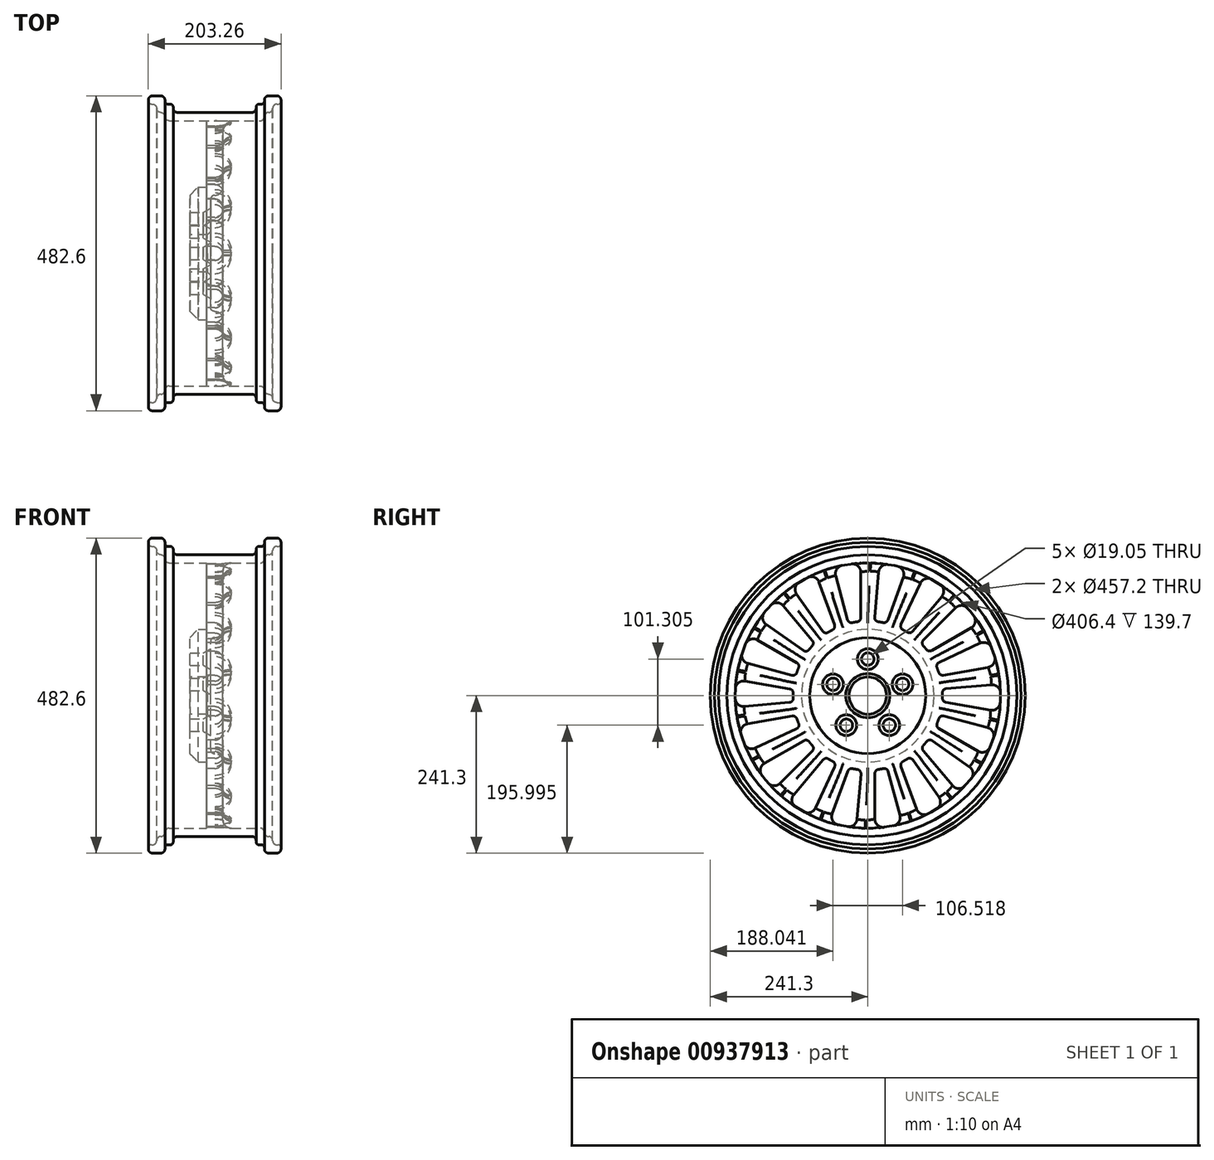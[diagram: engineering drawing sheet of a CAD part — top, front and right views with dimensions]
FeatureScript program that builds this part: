
annotation { "Feature Type Name" : "Feature", "Feature Type Description" : "" }
export const myFeature = defineFeature(function(context is Context, id is Id, definition is map)
    precondition{}
    {
        {
            var Q0;
            Q0=qCreatedBy(makeId("Front.planeOp"),FACE);
            var sketch = newSketch(context, id + "F0", { "sketchPlane" : qUnion([Q0])});
            skLineSegment(sketch, "E0", {"start": v(12.7, 101.6) * mm, "end": v(12.7, 203.2) * mm});
            skLineSegment(sketch, "E1", {"start": v(95.25, 241.3) * mm, "end": v(82.55, 241.3) * mm});
            skLineSegment(sketch, "E2", {"start": v(76.2, 234.95) * mm, "end": v(76.2, 233.05) * mm});
            skLineSegment(sketch, "E3", {"start": v(71.75, 228.6) * mm, "end": v(67.95, 228.6) * mm});
            skLineSegment(sketch, "E4", {"start": v(63.5, 224.16) * mm, "end": v(63.5, 222.25) * mm});
            skPoint(sketch, "E5.visualSharp", {"position": v(63.5, 215.9) * mm});
            skArc(sketch, "E5.filletArc", {"start": v(57.15, 215.9) * mm, "mid": v(61.64, 217.76) * mm, "end": v(63.5, 222.25) * mm});
            skPoint(sketch, "E6.visualSharp", {"position": v(63.5, 228.6) * mm});
            skArc(sketch, "E6.filletArc", {"start": v(67.95, 228.6) * mm, "mid": v(64.8, 227.3) * mm, "end": v(63.5, 224.16) * mm});
            skPoint(sketch, "E7.visualSharp", {"position": v(76.2, 228.6) * mm});
            skArc(sketch, "E7.filletArc", {"start": v(71.75, 228.6) * mm, "mid": v(74.9, 229.9) * mm, "end": v(76.2, 233.05) * mm});
            skPoint(sketch, "E8.visualSharp", {"position": v(76.2, 241.3) * mm});
            skArc(sketch, "E8.filletArc", {"start": v(82.55, 241.3) * mm, "mid": v(78.06, 239.44) * mm, "end": v(76.2, 234.95) * mm});
            skPoint(sketch, "E9.visualSharp", {"position": v(101.6, 241.3) * mm});
            skArc(sketch, "E9.filletArc", {"start": v(101.6, 234.95) * mm, "mid": v(99.74, 239.44) * mm, "end": v(95.25, 241.3) * mm});
            skLineSegment(sketch, "E10", {"start": v(12.7, 203.2) * mm, "end": v(69.85, 203.2) * mm});
            skLineSegment(sketch, "E11", {"start": v(76.2, 209.55) * mm, "end": v(76.2, 209.55) * mm});
            skLineSegment(sketch, "E12", {"start": v(82.55, 215.9) * mm, "end": v(82.55, 215.9) * mm});
            skPoint(sketch, "E12.endSnap0", {"position": v(88.9, 241.3) * mm});
            skLineSegment(sketch, "E13", {"start": v(88.9, 222.25) * mm, "end": v(88.9, 222.25) * mm});
            skLineSegment(sketch, "E14", {"start": v(95.25, 228.6) * mm, "end": v(97.18, 228.6) * mm});
            skLineSegment(sketch, "E15", {"start": v(101.63, 233.1) * mm, "end": v(101.6, 234.95) * mm});
            skPoint(sketch, "E16.visualSharp", {"position": v(76.2, 203.2) * mm});
            skArc(sketch, "E16.filletArc", {"start": v(69.85, 203.2) * mm, "mid": v(74.34, 205.06) * mm, "end": v(76.2, 209.55) * mm});
            skPoint(sketch, "E17.visualSharp", {"position": v(88.9, 215.9) * mm});
            skArc(sketch, "E17.filletArc", {"start": v(82.55, 215.9) * mm, "mid": v(87.04, 217.76) * mm, "end": v(88.9, 222.25) * mm});
            skPoint(sketch, "E18.visualSharp", {"position": v(88.9, 228.6) * mm});
            skArc(sketch, "E18.filletArc", {"start": v(95.25, 228.6) * mm, "mid": v(90.76, 226.74) * mm, "end": v(88.9, 222.25) * mm});
            skPoint(sketch, "E19.visualSharp", {"position": v(76.2, 215.9) * mm});
            skArc(sketch, "E19.filletArc", {"start": v(82.55, 215.9) * mm, "mid": v(78.06, 214.04) * mm, "end": v(76.2, 209.55) * mm});
            skPoint(sketch, "E20.visualSharp", {"position": v(101.7, 228.6) * mm});
            skArc(sketch, "E20.filletArc", {"start": v(97.18, 228.6) * mm, "mid": v(100.35, 229.92) * mm, "end": v(101.63, 233.1) * mm});
            skArc(sketch, "E21.MirrorCS", {"start": v(-82.55, 215.9) * mm, "mid": v(-87.04, 217.76) * mm, "end": v(-88.9, 222.25) * mm});
            skArc(sketch, "E22.MirrorCS", {"start": v(-71.75, 228.6) * mm, "mid": v(-74.9, 229.9) * mm, "end": v(-76.2, 233.05) * mm});
            skLineSegment(sketch, "E23.MirrorCS", {"start": v(-63.5, 224.16) * mm, "end": v(-63.5, 222.25) * mm});
            skLineSegment(sketch, "E24.MirrorCS", {"start": v(-76.2, 234.95) * mm, "end": v(-76.2, 233.05) * mm});
            skArc(sketch, "E25.MirrorCS", {"start": v(-97.18, 228.6) * mm, "mid": v(-100.35, 229.92) * mm, "end": v(-101.63, 233.1) * mm});
            skArc(sketch, "E26.MirrorCS", {"start": v(-95.25, 228.6) * mm, "mid": v(-90.76, 226.74) * mm, "end": v(-88.9, 222.25) * mm});
            skLineSegment(sketch, "E27.MirrorCS", {"start": v(-101.63, 233.1) * mm, "end": v(-101.6, 234.95) * mm});
            skLineSegment(sketch, "E28.MirrorCS", {"start": v(-95.25, 228.6) * mm, "end": v(-97.18, 228.6) * mm});
            skArc(sketch, "E29.MirrorCS", {"start": v(-69.85, 203.2) * mm, "mid": v(-74.34, 205.06) * mm, "end": v(-76.2, 209.55) * mm});
            skArc(sketch, "E30.MirrorCS", {"start": v(-101.6, 234.95) * mm, "mid": v(-99.74, 239.44) * mm, "end": v(-95.25, 241.3) * mm});
            skLineSegment(sketch, "E31.MirrorCS", {"start": v(-71.75, 228.6) * mm, "end": v(-67.95, 228.6) * mm});
            skArc(sketch, "E32.MirrorCS", {"start": v(-82.55, 215.9) * mm, "mid": v(-78.06, 214.04) * mm, "end": v(-76.2, 209.55) * mm});
            skArc(sketch, "E33.MirrorCS", {"start": v(-82.55, 241.3) * mm, "mid": v(-78.06, 239.44) * mm, "end": v(-76.2, 234.95) * mm});
            skLineSegment(sketch, "E34.MirrorCS", {"start": v(-95.25, 241.3) * mm, "end": v(-82.55, 241.3) * mm});
            skArc(sketch, "E35.MirrorCS", {"start": v(-67.95, 228.6) * mm, "mid": v(-64.8, 227.3) * mm, "end": v(-63.5, 224.16) * mm});
            skArc(sketch, "E36.MirrorCS", {"start": v(-57.15, 215.9) * mm, "mid": v(-61.64, 217.76) * mm, "end": v(-63.5, 222.25) * mm});
            skLineSegment(sketch, "E37.MirrorCS", {"start": v(-82.55, 215.9) * mm, "end": v(-82.55, 215.9) * mm});
            skPoint(sketch, "E38.MirrorP", {"position": v(-63.5, 215.9) * mm});
            skPoint(sketch, "E39.MirrorP", {"position": v(-88.9, 215.9) * mm});
            skPoint(sketch, "E40.MirrorP", {"position": v(-76.2, 215.9) * mm});
            skPoint(sketch, "E41.MirrorP", {"position": v(-88.9, 228.6) * mm});
            skPoint(sketch, "E42.MirrorP", {"position": v(-76.2, 228.6) * mm});
            skPoint(sketch, "E43.MirrorP", {"position": v(-76.2, 241.3) * mm});
            skLineSegment(sketch, "E44.MirrorCS", {"start": v(-12.7, 101.6) * mm, "end": v(-12.7, 203.2) * mm});
            skPoint(sketch, "E45.MirrorP", {"position": v(-76.2, 203.2) * mm});
            skLineSegment(sketch, "E46.MirrorCS", {"start": v(-88.9, 222.25) * mm, "end": v(-88.9, 222.25) * mm});
            skPoint(sketch, "E47.MirrorP", {"position": v(-101.7, 228.6) * mm});
            skLineSegment(sketch, "E48.MirrorCS", {"start": v(-12.7, 203.2) * mm, "end": v(-69.85, 203.2) * mm});
            skPoint(sketch, "E49.MirrorP", {"position": v(-101.6, 241.3) * mm});
            skPoint(sketch, "E50.MirrorP", {"position": v(-63.5, 228.6) * mm});
            skPoint(sketch, "E51.MirrorP", {"position": v(-88.9, 241.3) * mm});
            skLineSegment(sketch, "E52.MirrorCS", {"start": v(-76.2, 209.55) * mm, "end": v(-76.2, 209.55) * mm});
            skLineSegment(sketch, "E53", {"start": v(-38.1, 28.65) * mm, "end": v(-38.1, 101.6) * mm});
            skLineSegment(sketch, "E54", {"start": v(-38.1, 101.6) * mm, "end": v(-12.7, 101.6) * mm});
            skPoint(sketch, "E55.orphan", {"position": v(0, 0) * mm});
            skLineSegment(sketch, "E56.trimOffspring", {"start": v(0, 88.9) * mm, "end": v(0, 88.9) * mm});
            skLineSegment(sketch, "E57", {"start": v(-6.35, 28.57) * mm, "end": v(-6.35, 82.55) * mm});
            skPoint(sketch, "E58.newPointA", {"position": v(-6.35, 88.9) * mm});
            skPoint(sketch, "E58.newPointB", {"position": v(-4.35, 88.9) * mm});
            skArc(sketch, "E58.filletArc", {"start": v(0, 88.9) * mm, "mid": v(-4.5, 87.04) * mm, "end": v(-6.35, 82.55) * mm});
            skPoint(sketch, "E59.visualSharp", {"position": v(12.7, 88.9) * mm});
            skArc(sketch, "E59.filletArc", {"start": v(0, 88.9) * mm, "mid": v(8.98, 92.62) * mm, "end": v(12.7, 101.6) * mm});
            skLineSegment(sketch, "E60", {"start": v(-6.35, 28.57) * mm, "end": v(-38.1, 28.65) * mm});
            skLineSegment(sketch, "E61", {"start": v(57.15, 215.9) * mm, "end": v(-57.15, 215.9) * mm});
            skLineSegment(sketch, "E62", {"start": v(0, 0) * mm, "end": v(-39.67, 0) * mm});
            skSolve(sketch);
        }
        {
            var Q0;
            Q0 = qSketchRegion(id + "F0", true);
            var Q1;
            Q1=sQuery(id+"F0.wireOp",EDGE,"E62");
            revolve(context, id + "F1", {"surfaceOperationType" : NewSurfaceOperationType.NEW, "entities" : qUnion([Q0]), "axis" : qUnion([Q1]), "revolveType" : RevolveType.FULL});
        }
        {
            var Q0;
            Q0=makeQuery(id+"F1.opRevolve","SWEPT_FACE",FACE,{"disambiguationData":[OSD([sQuery(id+"F0.wireOp",EDGE,"E44.MirrorCS")])]});
            var sketch = newSketch(context, id + "F2", { "sketchPlane" : qUnion([Q0])});
            skArc(sketch, "E63", {"start": v(39.39, 199.35) * mm, "mid": v(32.22, 200.63) * mm, "end": v(25.02, 201.65) * mm});
            skArc(sketch, "E64", {"start": v(23.73, 111.8) * mm, "mid": v(19.98, 112.54) * mm, "end": v(16.2, 113.15) * mm});
            skLineSegment(sketch, "E65", {"start": v(10.75, 189.05) * mm, "end": v(10.75, 119.43) * mm});
            skLineSegment(sketch, "E66", {"start": v(31.18, 116.38) * mm, "end": v(49.2, 183.6) * mm});
            skPoint(sketch, "E67.visualSharp", {"position": v(10.75, 113.8) * mm});
            skArc(sketch, "E67.filletArc", {"start": v(10.75, 119.43) * mm, "mid": v(12.3, 115.27) * mm, "end": v(16.2, 113.15) * mm});
            skPoint(sketch, "E68.visualSharp", {"position": v(29.58, 110.4) * mm});
            skArc(sketch, "E68.filletArc", {"start": v(23.73, 111.8) * mm, "mid": v(28.37, 112.6) * mm, "end": v(31.18, 116.38) * mm});
            skPoint(sketch, "E69.visualSharp", {"position": v(52.6, 196.28) * mm});
            skArc(sketch, "E69.filletArc", {"start": v(49.2, 183.6) * mm, "mid": v(47.7, 193.6) * mm, "end": v(39.39, 199.35) * mm});
            skPoint(sketch, "E70.visualSharp", {"position": v(10.75, 202.92) * mm});
            skArc(sketch, "E70.filletArc", {"start": v(25.02, 201.65) * mm, "mid": v(15.04, 198.57) * mm, "end": v(10.75, 189.05) * mm});
            skPoint(sketch, "E71.1.0", {"position": v(-28.82, 110.6) * mm});
            skLineSegment(sketch, "E71.1.1", {"start": v(-54.56, 181.33) * mm, "end": v(-30.74, 115.9) * mm});
            skPoint(sketch, "E71.1.2", {"position": v(-9.96, 113.87) * mm});
            skPoint(sketch, "E71.1.3", {"position": v(-59.3, 194.36) * mm});
            skLineSegment(sketch, "E71.1.4", {"start": v(-10.5, 120.02) * mm, "end": v(-16.57, 189.35) * mm});
            skPoint(sketch, "E71.1.5", {"position": v(-17.71, 202.43) * mm});
            skArc(sketch, "E71.1.6", {"start": v(-16.57, 189.35) * mm, "mid": v(-21.38, 198.24) * mm, "end": v(-31.17, 200.8) * mm});
            skArc(sketch, "E71.1.7", {"start": v(-45.46, 198.05) * mm, "mid": v(-53.78, 191.74) * mm, "end": v(-54.56, 181.33) * mm});
            skArc(sketch, "E71.1.8", {"start": v(-31.17, 200.8) * mm, "mid": v(-38.34, 199.55) * mm, "end": v(-45.46, 198.05) * mm});
            skArc(sketch, "E71.1.9", {"start": v(-30.74, 115.9) * mm, "mid": v(-27.86, 112.53) * mm, "end": v(-23.47, 111.86) * mm});
            skArc(sketch, "E71.1.10", {"start": v(-15.94, 113.18) * mm, "mid": v(-19.72, 112.59) * mm, "end": v(-23.47, 111.86) * mm});
            skArc(sketch, "E71.1.11", {"start": v(-15.94, 113.18) * mm, "mid": v(-11.86, 115.52) * mm, "end": v(-10.5, 120.02) * mm});
            skPoint(sketch, "E71.2.0", {"position": v(-64.9, 94.08) * mm});
            skLineSegment(sketch, "E71.2.1", {"start": v(-113.28, 151.73) * mm, "end": v(-68.53, 98.4) * mm});
            skPoint(sketch, "E71.2.2", {"position": v(-48.3, 103.6) * mm});
            skPoint(sketch, "E71.2.3", {"position": v(-122.2, 162.35) * mm});
            skLineSegment(sketch, "E71.2.4", {"start": v(-50.92, 109.2) * mm, "end": v(-80.33, 172.27) * mm});
            skPoint(sketch, "E71.2.5", {"position": v(-85.88, 184.16) * mm});
            skArc(sketch, "E71.2.6", {"start": v(-80.33, 172.27) * mm, "mid": v(-87.9, 178.97) * mm, "end": v(-97.96, 178.03) * mm});
            skArc(sketch, "E71.2.7", {"start": v(-110.46, 170.56) * mm, "mid": v(-116.11, 161.78) * mm, "end": v(-113.28, 151.73) * mm});
            skArc(sketch, "E71.2.8", {"start": v(-97.96, 178.03) * mm, "mid": v(-104.28, 174.4) * mm, "end": v(-110.46, 170.56) * mm});
            skArc(sketch, "E71.2.9", {"start": v(-68.53, 98.4) * mm, "mid": v(-64.67, 96.21) * mm, "end": v(-60.32, 97.09) * mm});
            skArc(sketch, "E71.2.10", {"start": v(-53.7, 100.9) * mm, "mid": v(-57.04, 99.05) * mm, "end": v(-60.32, 97.09) * mm});
            skArc(sketch, "E71.2.11", {"start": v(-53.7, 100.9) * mm, "mid": v(-50.65, 104.5) * mm, "end": v(-50.92, 109.2) * mm});
            skPoint(sketch, "E71.3.0", {"position": v(-93.17, 66.2) * mm});
            skLineSegment(sketch, "E71.3.1", {"start": v(-158.35, 103.84) * mm, "end": v(-98.06, 69.03) * mm});
            skPoint(sketch, "E71.3.2", {"position": v(-80.82, 80.82) * mm});
            skPoint(sketch, "E71.3.3", {"position": v(-170.35, 110.77) * mm});
            skLineSegment(sketch, "E71.3.4", {"start": v(-85.2, 85.2) * mm, "end": v(-134.4, 134.4) * mm});
            skPoint(sketch, "E71.3.5", {"position": v(-143.68, 143.68) * mm});
            skArc(sketch, "E71.3.6", {"start": v(-134.4, 134.4) * mm, "mid": v(-143.8, 138.12) * mm, "end": v(-152.94, 133.79) * mm});
            skArc(sketch, "E71.3.7", {"start": v(-162.13, 122.5) * mm, "mid": v(-164.44, 112.31) * mm, "end": v(-158.35, 103.84) * mm});
            skArc(sketch, "E71.3.8", {"start": v(-152.94, 133.79) * mm, "mid": v(-157.64, 128.22) * mm, "end": v(-162.13, 122.5) * mm});
            skArc(sketch, "E71.3.9", {"start": v(-98.06, 69.03) * mm, "mid": v(-93.68, 68.3) * mm, "end": v(-89.89, 70.6) * mm});
            skArc(sketch, "E71.3.10", {"start": v(-84.96, 76.46) * mm, "mid": v(-87.47, 73.57) * mm, "end": v(-89.89, 70.6) * mm});
            skArc(sketch, "E71.3.11", {"start": v(-84.96, 76.46) * mm, "mid": v(-83.34, 80.87) * mm, "end": v(-85.2, 85.2) * mm});
            skPoint(sketch, "E71.4.0", {"position": v(-110.2, 30.35) * mm});
            skLineSegment(sketch, "E71.4.1", {"start": v(-184.31, 43.42) * mm, "end": v(-115.75, 31.33) * mm});
            skPoint(sketch, "E71.4.2", {"position": v(-103.6, 48.3) * mm});
            skPoint(sketch, "E71.4.3", {"position": v(-197.97, 45.82) * mm});
            skLineSegment(sketch, "E71.4.4", {"start": v(-109.2, 50.92) * mm, "end": v(-172.27, 80.33) * mm});
            skPoint(sketch, "E71.4.5", {"position": v(-184.16, 85.88) * mm});
            skArc(sketch, "E71.4.6", {"start": v(-172.27, 80.33) * mm, "mid": v(-182.37, 80.6) * mm, "end": v(-189.48, 73.4) * mm});
            skArc(sketch, "E71.4.7", {"start": v(-194.25, 59.65) * mm, "mid": v(-192.94, 49.3) * mm, "end": v(-184.31, 43.42) * mm});
            skArc(sketch, "E71.4.8", {"start": v(-189.48, 73.4) * mm, "mid": v(-191.99, 66.57) * mm, "end": v(-194.25, 59.65) * mm});
            skArc(sketch, "E71.4.9", {"start": v(-115.75, 31.33) * mm, "mid": v(-111.38, 32.13) * mm, "end": v(-108.61, 35.6) * mm});
            skArc(sketch, "E71.4.10", {"start": v(-105.99, 42.79) * mm, "mid": v(-107.36, 39.22) * mm, "end": v(-108.61, 35.6) * mm});
            skArc(sketch, "E71.4.11", {"start": v(-105.99, 42.79) * mm, "mid": v(-105.97, 47.5) * mm, "end": v(-109.2, 50.92) * mm});
            skPoint(sketch, "E71.5.0", {"position": v(-113.93, -9.17) * mm});
            skLineSegment(sketch, "E71.5.1", {"start": v(-188.05, -22.24) * mm, "end": v(-119.48, -10.15) * mm});
            skPoint(sketch, "E71.5.2", {"position": v(-113.87, 9.96) * mm});
            skPoint(sketch, "E71.5.3", {"position": v(-201.7, -24.65) * mm});
            skLineSegment(sketch, "E71.5.4", {"start": v(-120.02, 10.5) * mm, "end": v(-189.35, 16.57) * mm});
            skPoint(sketch, "E71.5.5", {"position": v(-202.43, 17.71) * mm});
            skArc(sketch, "E71.5.6", {"start": v(-189.35, 16.57) * mm, "mid": v(-198.94, 13.37) * mm, "end": v(-203.16, 4.18) * mm});
            skArc(sketch, "E71.5.7", {"start": v(-202.93, -10.38) * mm, "mid": v(-198.16, -19.67) * mm, "end": v(-188.05, -22.24) * mm});
            skArc(sketch, "E71.5.8", {"start": v(-203.16, 4.18) * mm, "mid": v(-203.18, -3.1) * mm, "end": v(-202.93, -10.38) * mm});
            skArc(sketch, "E71.5.9", {"start": v(-119.48, -10.15) * mm, "mid": v(-115.66, -7.9) * mm, "end": v(-114.24, -3.7) * mm});
            skArc(sketch, "E71.5.10", {"start": v(-114.23, 3.96) * mm, "mid": v(-114.3, 0.13) * mm, "end": v(-114.24, -3.7) * mm});
            skArc(sketch, "E71.5.11", {"start": v(-114.23, 3.96) * mm, "mid": v(-115.82, 8.38) * mm, "end": v(-120.02, 10.5) * mm});
            skPoint(sketch, "E71.6.0", {"position": v(-103.92, -47.59) * mm});
            skLineSegment(sketch, "E71.6.1", {"start": v(-169.1, -85.21) * mm, "end": v(-108.8, -50.4) * mm});
            skPoint(sketch, "E71.6.2", {"position": v(-110.4, -29.58) * mm});
            skPoint(sketch, "E71.6.3", {"position": v(-181.1, -92.15) * mm});
            skLineSegment(sketch, "E71.6.4", {"start": v(-116.38, -31.18) * mm, "end": v(-183.6, -49.2) * mm});
            skPoint(sketch, "E71.6.5", {"position": v(-196.28, -52.6) * mm});
            skArc(sketch, "E71.6.6", {"start": v(-183.6, -49.2) * mm, "mid": v(-191.52, -55.48) * mm, "end": v(-192.33, -65.56) * mm});
            skArc(sketch, "E71.6.7", {"start": v(-187.15, -79.16) * mm, "mid": v(-179.49, -86.26) * mm, "end": v(-169.1, -85.21) * mm});
            skArc(sketch, "E71.6.8", {"start": v(-192.33, -65.56) * mm, "mid": v(-189.86, -72.4) * mm, "end": v(-187.15, -79.16) * mm});
            skArc(sketch, "E71.6.9", {"start": v(-108.8, -50.4) * mm, "mid": v(-105.98, -46.98) * mm, "end": v(-106.09, -42.54) * mm});
            skArc(sketch, "E71.6.10", {"start": v(-108.7, -35.35) * mm, "mid": v(-107.45, -38.97) * mm, "end": v(-106.09, -42.54) * mm});
            skArc(sketch, "E71.6.11", {"start": v(-108.7, -35.35) * mm, "mid": v(-111.7, -31.74) * mm, "end": v(-116.38, -31.18) * mm});
            skPoint(sketch, "E71.7.0", {"position": v(-81.38, -80.26) * mm});
            skLineSegment(sketch, "E71.7.1", {"start": v(-129.76, -137.91) * mm, "end": v(-85, -84.58) * mm});
            skPoint(sketch, "E71.7.2", {"position": v(-93.63, -65.56) * mm});
            skPoint(sketch, "E71.7.3", {"position": v(-138.67, -148.53) * mm});
            skLineSegment(sketch, "E71.7.4", {"start": v(-98.7, -69.1) * mm, "end": v(-155.7, -109.02) * mm});
            skPoint(sketch, "E71.7.5", {"position": v(-166.45, -116.55) * mm});
            skArc(sketch, "E71.7.6", {"start": v(-155.7, -109.02) * mm, "mid": v(-161, -117.64) * mm, "end": v(-158.31, -127.39) * mm});
            skArc(sketch, "E71.7.7", {"start": v(-148.78, -138.4) * mm, "mid": v(-139.16, -142.44) * mm, "end": v(-129.76, -137.91) * mm});
            skArc(sketch, "E71.7.8", {"start": v(-158.31, -127.39) * mm, "mid": v(-153.65, -132.98) * mm, "end": v(-148.78, -138.4) * mm});
            skArc(sketch, "E71.7.9", {"start": v(-85, -84.58) * mm, "mid": v(-83.52, -80.4) * mm, "end": v(-85.14, -76.26) * mm});
            skArc(sketch, "E71.7.10", {"start": v(-90.05, -70.4) * mm, "mid": v(-87.64, -73.37) * mm, "end": v(-85.14, -76.26) * mm});
            skArc(sketch, "E71.7.11", {"start": v(-90.05, -70.4) * mm, "mid": v(-94.11, -68.03) * mm, "end": v(-98.7, -69.1) * mm});
            skPoint(sketch, "E71.8.0", {"position": v(-49.02, -103.25) * mm});
            skLineSegment(sketch, "E71.8.1", {"start": v(-74.76, -173.97) * mm, "end": v(-50.95, -108.55) * mm});
            skPoint(sketch, "E71.8.2", {"position": v(-65.56, -93.63) * mm});
            skPoint(sketch, "E71.8.3", {"position": v(-79.5, -187) * mm});
            skLineSegment(sketch, "E71.8.4", {"start": v(-69.1, -98.7) * mm, "end": v(-109.02, -155.7) * mm});
            skPoint(sketch, "E71.8.5", {"position": v(-116.55, -166.45) * mm});
            skArc(sketch, "E71.8.6", {"start": v(-109.02, -155.7) * mm, "mid": v(-111.05, -165.6) * mm, "end": v(-105.2, -173.85) * mm});
            skArc(sketch, "E71.8.7", {"start": v(-92.48, -180.94) * mm, "mid": v(-82.05, -181.45) * mm, "end": v(-74.76, -173.97) * mm});
            skArc(sketch, "E71.8.8", {"start": v(-105.2, -173.85) * mm, "mid": v(-98.9, -177.5) * mm, "end": v(-92.48, -180.94) * mm});
            skArc(sketch, "E71.8.9", {"start": v(-50.95, -108.55) * mm, "mid": v(-50.99, -104.11) * mm, "end": v(-53.92, -100.78) * mm});
            skArc(sketch, "E71.8.10", {"start": v(-60.54, -96.95) * mm, "mid": v(-57.26, -98.92) * mm, "end": v(-53.92, -100.78) * mm});
            skArc(sketch, "E71.8.11", {"start": v(-60.54, -96.95) * mm, "mid": v(-65.17, -96.11) * mm, "end": v(-69.1, -98.7) * mm});
            skPoint(sketch, "E71.9.0", {"position": v(-10.75, -113.8) * mm});
            skLineSegment(sketch, "E71.9.1", {"start": v(-10.75, -189.05) * mm, "end": v(-10.75, -119.43) * mm});
            skPoint(sketch, "E71.9.2", {"position": v(-29.58, -110.4) * mm});
            skPoint(sketch, "E71.9.3", {"position": v(-10.75, -202.92) * mm});
            skLineSegment(sketch, "E71.9.4", {"start": v(-31.18, -116.38) * mm, "end": v(-49.2, -183.6) * mm});
            skPoint(sketch, "E71.9.5", {"position": v(-52.6, -196.28) * mm});
            skArc(sketch, "E71.9.6", {"start": v(-49.2, -183.6) * mm, "mid": v(-47.7, -193.6) * mm, "end": v(-39.39, -199.35) * mm});
            skArc(sketch, "E71.9.7", {"start": v(-25.02, -201.65) * mm, "mid": v(-15.04, -198.57) * mm, "end": v(-10.75, -189.05) * mm});
            skArc(sketch, "E71.9.8", {"start": v(-39.39, -199.35) * mm, "mid": v(-32.22, -200.63) * mm, "end": v(-25.02, -201.65) * mm});
            skArc(sketch, "E71.9.9", {"start": v(-10.75, -119.43) * mm, "mid": v(-12.3, -115.27) * mm, "end": v(-16.2, -113.15) * mm});
            skArc(sketch, "E71.9.10", {"start": v(-23.73, -111.8) * mm, "mid": v(-19.98, -112.54) * mm, "end": v(-16.2, -113.15) * mm});
            skArc(sketch, "E71.9.11", {"start": v(-23.73, -111.8) * mm, "mid": v(-28.37, -112.6) * mm, "end": v(-31.18, -116.38) * mm});
            skPoint(sketch, "E71.10.0", {"position": v(28.82, -110.6) * mm});
            skLineSegment(sketch, "E71.10.1", {"start": v(54.56, -181.33) * mm, "end": v(30.74, -115.9) * mm});
            skPoint(sketch, "E71.10.2", {"position": v(9.96, -113.87) * mm});
            skPoint(sketch, "E71.10.3", {"position": v(59.3, -194.36) * mm});
            skLineSegment(sketch, "E71.10.4", {"start": v(10.5, -120.02) * mm, "end": v(16.57, -189.35) * mm});
            skPoint(sketch, "E71.10.5", {"position": v(17.71, -202.43) * mm});
            skArc(sketch, "E71.10.6", {"start": v(16.57, -189.35) * mm, "mid": v(21.38, -198.24) * mm, "end": v(31.17, -200.8) * mm});
            skArc(sketch, "E71.10.7", {"start": v(45.46, -198.05) * mm, "mid": v(53.78, -191.74) * mm, "end": v(54.56, -181.33) * mm});
            skArc(sketch, "E71.10.8", {"start": v(31.17, -200.8) * mm, "mid": v(38.34, -199.55) * mm, "end": v(45.46, -198.05) * mm});
            skArc(sketch, "E71.10.9", {"start": v(30.74, -115.9) * mm, "mid": v(27.86, -112.53) * mm, "end": v(23.47, -111.86) * mm});
            skArc(sketch, "E71.10.10", {"start": v(15.94, -113.18) * mm, "mid": v(19.72, -112.59) * mm, "end": v(23.47, -111.86) * mm});
            skArc(sketch, "E71.10.11", {"start": v(15.94, -113.18) * mm, "mid": v(11.86, -115.52) * mm, "end": v(10.5, -120.02) * mm});
            skPoint(sketch, "E71.11.0", {"position": v(64.9, -94.08) * mm});
            skLineSegment(sketch, "E71.11.1", {"start": v(113.28, -151.73) * mm, "end": v(68.53, -98.4) * mm});
            skPoint(sketch, "E71.11.2", {"position": v(48.3, -103.6) * mm});
            skPoint(sketch, "E71.11.3", {"position": v(122.2, -162.35) * mm});
            skLineSegment(sketch, "E71.11.4", {"start": v(50.92, -109.2) * mm, "end": v(80.33, -172.27) * mm});
            skPoint(sketch, "E71.11.5", {"position": v(85.88, -184.16) * mm});
            skArc(sketch, "E71.11.6", {"start": v(80.33, -172.27) * mm, "mid": v(87.9, -178.97) * mm, "end": v(97.96, -178.03) * mm});
            skArc(sketch, "E71.11.7", {"start": v(110.46, -170.56) * mm, "mid": v(116.11, -161.78) * mm, "end": v(113.28, -151.73) * mm});
            skArc(sketch, "E71.11.8", {"start": v(97.96, -178.03) * mm, "mid": v(104.28, -174.4) * mm, "end": v(110.46, -170.56) * mm});
            skArc(sketch, "E71.11.9", {"start": v(68.53, -98.4) * mm, "mid": v(64.67, -96.21) * mm, "end": v(60.32, -97.09) * mm});
            skArc(sketch, "E71.11.10", {"start": v(53.7, -100.9) * mm, "mid": v(57.04, -99.05) * mm, "end": v(60.32, -97.09) * mm});
            skArc(sketch, "E71.11.11", {"start": v(53.7, -100.9) * mm, "mid": v(50.65, -104.5) * mm, "end": v(50.92, -109.2) * mm});
            skPoint(sketch, "E71.12.0", {"position": v(93.17, -66.2) * mm});
            skLineSegment(sketch, "E71.12.1", {"start": v(158.35, -103.84) * mm, "end": v(98.06, -69.03) * mm});
            skPoint(sketch, "E71.12.2", {"position": v(80.82, -80.82) * mm});
            skPoint(sketch, "E71.12.3", {"position": v(170.35, -110.77) * mm});
            skLineSegment(sketch, "E71.12.4", {"start": v(85.2, -85.2) * mm, "end": v(134.4, -134.4) * mm});
            skPoint(sketch, "E71.12.5", {"position": v(143.68, -143.68) * mm});
            skArc(sketch, "E71.12.6", {"start": v(134.4, -134.4) * mm, "mid": v(143.8, -138.12) * mm, "end": v(152.94, -133.79) * mm});
            skArc(sketch, "E71.12.7", {"start": v(162.13, -122.5) * mm, "mid": v(164.44, -112.31) * mm, "end": v(158.35, -103.84) * mm});
            skArc(sketch, "E71.12.8", {"start": v(152.94, -133.79) * mm, "mid": v(157.64, -128.22) * mm, "end": v(162.13, -122.5) * mm});
            skArc(sketch, "E71.12.9", {"start": v(98.06, -69.03) * mm, "mid": v(93.68, -68.3) * mm, "end": v(89.89, -70.6) * mm});
            skArc(sketch, "E71.12.10", {"start": v(84.96, -76.46) * mm, "mid": v(87.47, -73.57) * mm, "end": v(89.89, -70.6) * mm});
            skArc(sketch, "E71.12.11", {"start": v(84.96, -76.46) * mm, "mid": v(83.34, -80.87) * mm, "end": v(85.2, -85.2) * mm});
            skPoint(sketch, "E71.13.0", {"position": v(110.2, -30.35) * mm});
            skLineSegment(sketch, "E71.13.1", {"start": v(184.31, -43.42) * mm, "end": v(115.75, -31.33) * mm});
            skPoint(sketch, "E71.13.2", {"position": v(103.6, -48.3) * mm});
            skPoint(sketch, "E71.13.3", {"position": v(197.97, -45.82) * mm});
            skLineSegment(sketch, "E71.13.4", {"start": v(109.2, -50.92) * mm, "end": v(172.27, -80.33) * mm});
            skPoint(sketch, "E71.13.5", {"position": v(184.16, -85.88) * mm});
            skArc(sketch, "E71.13.6", {"start": v(172.27, -80.33) * mm, "mid": v(182.37, -80.6) * mm, "end": v(189.48, -73.4) * mm});
            skArc(sketch, "E71.13.7", {"start": v(194.25, -59.65) * mm, "mid": v(192.94, -49.3) * mm, "end": v(184.31, -43.42) * mm});
            skArc(sketch, "E71.13.8", {"start": v(189.48, -73.4) * mm, "mid": v(191.99, -66.57) * mm, "end": v(194.25, -59.65) * mm});
            skArc(sketch, "E71.13.9", {"start": v(115.75, -31.33) * mm, "mid": v(111.38, -32.13) * mm, "end": v(108.61, -35.6) * mm});
            skArc(sketch, "E71.13.10", {"start": v(105.99, -42.79) * mm, "mid": v(107.36, -39.22) * mm, "end": v(108.61, -35.6) * mm});
            skArc(sketch, "E71.13.11", {"start": v(105.99, -42.79) * mm, "mid": v(105.97, -47.5) * mm, "end": v(109.2, -50.92) * mm});
            skPoint(sketch, "E71.14.0", {"position": v(113.93, 9.17) * mm});
            skLineSegment(sketch, "E71.14.1", {"start": v(188.05, 22.24) * mm, "end": v(119.48, 10.15) * mm});
            skPoint(sketch, "E71.14.2", {"position": v(113.87, -9.96) * mm});
            skPoint(sketch, "E71.14.3", {"position": v(201.7, 24.65) * mm});
            skLineSegment(sketch, "E71.14.4", {"start": v(120.02, -10.5) * mm, "end": v(189.35, -16.57) * mm});
            skPoint(sketch, "E71.14.5", {"position": v(202.43, -17.71) * mm});
            skArc(sketch, "E71.14.6", {"start": v(189.35, -16.57) * mm, "mid": v(198.94, -13.37) * mm, "end": v(203.16, -4.18) * mm});
            skArc(sketch, "E71.14.7", {"start": v(202.93, 10.38) * mm, "mid": v(198.16, 19.67) * mm, "end": v(188.05, 22.24) * mm});
            skArc(sketch, "E71.14.8", {"start": v(203.16, -4.18) * mm, "mid": v(203.18, 3.1) * mm, "end": v(202.93, 10.38) * mm});
            skArc(sketch, "E71.14.9", {"start": v(119.48, 10.15) * mm, "mid": v(115.66, 7.9) * mm, "end": v(114.24, 3.7) * mm});
            skArc(sketch, "E71.14.10", {"start": v(114.23, -3.96) * mm, "mid": v(114.3, -0.13) * mm, "end": v(114.24, 3.7) * mm});
            skArc(sketch, "E71.14.11", {"start": v(114.23, -3.96) * mm, "mid": v(115.82, -8.38) * mm, "end": v(120.02, -10.5) * mm});
            skPoint(sketch, "E71.15.0", {"position": v(103.92, 47.59) * mm});
            skLineSegment(sketch, "E71.15.1", {"start": v(169.1, 85.21) * mm, "end": v(108.8, 50.4) * mm});
            skPoint(sketch, "E71.15.2", {"position": v(110.4, 29.58) * mm});
            skPoint(sketch, "E71.15.3", {"position": v(181.1, 92.15) * mm});
            skLineSegment(sketch, "E71.15.4", {"start": v(116.38, 31.18) * mm, "end": v(183.6, 49.2) * mm});
            skPoint(sketch, "E71.15.5", {"position": v(196.28, 52.6) * mm});
            skArc(sketch, "E71.15.6", {"start": v(183.6, 49.2) * mm, "mid": v(191.52, 55.48) * mm, "end": v(192.33, 65.56) * mm});
            skArc(sketch, "E71.15.7", {"start": v(187.15, 79.16) * mm, "mid": v(179.49, 86.26) * mm, "end": v(169.1, 85.21) * mm});
            skArc(sketch, "E71.15.8", {"start": v(192.33, 65.56) * mm, "mid": v(189.86, 72.4) * mm, "end": v(187.15, 79.16) * mm});
            skArc(sketch, "E71.15.9", {"start": v(108.8, 50.4) * mm, "mid": v(105.98, 46.98) * mm, "end": v(106.09, 42.54) * mm});
            skArc(sketch, "E71.15.10", {"start": v(108.7, 35.35) * mm, "mid": v(107.45, 38.97) * mm, "end": v(106.09, 42.54) * mm});
            skArc(sketch, "E71.15.11", {"start": v(108.7, 35.35) * mm, "mid": v(111.7, 31.74) * mm, "end": v(116.38, 31.18) * mm});
            skPoint(sketch, "E71.16.0", {"position": v(81.38, 80.26) * mm});
            skLineSegment(sketch, "E71.16.1", {"start": v(129.76, 137.91) * mm, "end": v(85, 84.58) * mm});
            skPoint(sketch, "E71.16.2", {"position": v(93.63, 65.56) * mm});
            skPoint(sketch, "E71.16.3", {"position": v(138.67, 148.53) * mm});
            skLineSegment(sketch, "E71.16.4", {"start": v(98.7, 69.1) * mm, "end": v(155.7, 109.02) * mm});
            skPoint(sketch, "E71.16.5", {"position": v(166.45, 116.55) * mm});
            skArc(sketch, "E71.16.6", {"start": v(155.7, 109.02) * mm, "mid": v(161, 117.64) * mm, "end": v(158.31, 127.39) * mm});
            skArc(sketch, "E71.16.7", {"start": v(148.78, 138.4) * mm, "mid": v(139.16, 142.44) * mm, "end": v(129.76, 137.91) * mm});
            skArc(sketch, "E71.16.8", {"start": v(158.31, 127.39) * mm, "mid": v(153.65, 132.98) * mm, "end": v(148.78, 138.4) * mm});
            skArc(sketch, "E71.16.9", {"start": v(85, 84.58) * mm, "mid": v(83.52, 80.4) * mm, "end": v(85.14, 76.26) * mm});
            skArc(sketch, "E71.16.10", {"start": v(90.05, 70.4) * mm, "mid": v(87.64, 73.37) * mm, "end": v(85.14, 76.26) * mm});
            skArc(sketch, "E71.16.11", {"start": v(90.05, 70.4) * mm, "mid": v(94.11, 68.03) * mm, "end": v(98.7, 69.1) * mm});
            skPoint(sketch, "E71.17.0", {"position": v(49.02, 103.25) * mm});
            skLineSegment(sketch, "E71.17.1", {"start": v(74.76, 173.97) * mm, "end": v(50.95, 108.55) * mm});
            skPoint(sketch, "E71.17.2", {"position": v(65.56, 93.63) * mm});
            skPoint(sketch, "E71.17.3", {"position": v(79.5, 187) * mm});
            skLineSegment(sketch, "E71.17.4", {"start": v(69.1, 98.7) * mm, "end": v(109.02, 155.7) * mm});
            skPoint(sketch, "E71.17.5", {"position": v(116.55, 166.45) * mm});
            skArc(sketch, "E71.17.6", {"start": v(109.02, 155.7) * mm, "mid": v(111.05, 165.6) * mm, "end": v(105.2, 173.85) * mm});
            skArc(sketch, "E71.17.7", {"start": v(92.48, 180.94) * mm, "mid": v(82.05, 181.45) * mm, "end": v(74.76, 173.97) * mm});
            skArc(sketch, "E71.17.8", {"start": v(105.2, 173.85) * mm, "mid": v(98.9, 177.5) * mm, "end": v(92.48, 180.94) * mm});
            skArc(sketch, "E71.17.9", {"start": v(50.95, 108.55) * mm, "mid": v(50.99, 104.11) * mm, "end": v(53.92, 100.78) * mm});
            skArc(sketch, "E71.17.10", {"start": v(60.54, 96.95) * mm, "mid": v(57.26, 98.92) * mm, "end": v(53.92, 100.78) * mm});
            skArc(sketch, "E71.17.11", {"start": v(60.54, 96.95) * mm, "mid": v(65.17, 96.11) * mm, "end": v(69.1, 98.7) * mm});
            skSolve(sketch);
        }
        {
            var Q0;
            Q0 = qSketchRegion(id + "F2", true);
            extrude(context, id + "F3", {"entities" : qUnion([Q0]), "operationType" : NewBodyOperationType.REMOVE, "endBound" : BoundingType.SYMMETRIC, "oppositeDirection" : true, "depth" : 127 * mm, "offsetDistance" : 25.4 * mm});
        }
        {
            var Q0;
            Q0=makeQuery(id+"F1.opRevolve","SWEPT_FACE",FACE,{"disambiguationData":[OSD([sQuery(id+"F0.wireOp",EDGE,"E57")])]});
            var sketch = newSketch(context, id + "F4", { "sketchPlane" : qUnion([Q0])});
            skPoint(sketch, "E72", {"position": v(0, 56) * mm});
            skPoint(sketch, "E73.1.0", {"position": v(-53.26, 17.3) * mm});
            skPoint(sketch, "E73.2.0", {"position": v(-32.92, -45.3) * mm});
            skPoint(sketch, "E73.3.0", {"position": v(32.92, -45.3) * mm});
            skPoint(sketch, "E73.4.0", {"position": v(53.26, 17.3) * mm});
            skPoint(sketch, "E73.center", {"position": v(0, 0) * mm});
            skSolve(sketch);
        }
        {
            var Q0;
            Q0=sQuery(id+"F4.wireOp",VERTEX,"E72");
            var Q1;
            Q1=sQuery(id+"F4.wireOp",VERTEX,"E73.4.0");
            var Q2;
            Q2=sQuery(id+"F4.wireOp",VERTEX,"E73.3.0");
            var Q3;
            Q3=sQuery(id+"F4.wireOp",VERTEX,"E73.2.0");
            var Q4;
            Q4=sQuery(id+"F4.wireOp",VERTEX,"E73.1.0");
            var Q5;
            Q5=makeQuery(id+"F1.opRevolve","SWEPT_BODY",BODY,{"disambiguationData":[OSD([sQuery(id+"F0.wireOp",EDGE,"E0"),sQuery(id+"F0.wireOp",EDGE,"E1"),sQuery(id+"F0.wireOp",EDGE,"E2"),sQuery(id+"F0.wireOp",EDGE,"E3"),sQuery(id+"F0.wireOp",EDGE,"E4"),sQuery(id+"F0.wireOp",EDGE,"E5.filletArc"),sQuery(id+"F0.wireOp",EDGE,"E6.filletArc"),sQuery(id+"F0.wireOp",EDGE,"E7.filletArc"),sQuery(id+"F0.wireOp",EDGE,"E8.filletArc"),sQuery(id+"F0.wireOp",EDGE,"E9.filletArc"),sQuery(id+"F0.wireOp",EDGE,"E10"),sQuery(id+"F0.wireOp",EDGE,"E14"),sQuery(id+"F0.wireOp",EDGE,"E15"),sQuery(id+"F0.wireOp",EDGE,"E16.filletArc"),sQuery(id+"F0.wireOp",EDGE,"E17.filletArc"),sQuery(id+"F0.wireOp",EDGE,"E18.filletArc"),sQuery(id+"F0.wireOp",EDGE,"E19.filletArc"),sQuery(id+"F0.wireOp",EDGE,"E20.filletArc"),sQuery(id+"F0.wireOp",EDGE,"E21.MirrorCS"),sQuery(id+"F0.wireOp",EDGE,"E22.MirrorCS"),sQuery(id+"F0.wireOp",EDGE,"E23.MirrorCS"),sQuery(id+"F0.wireOp",EDGE,"E24.MirrorCS"),sQuery(id+"F0.wireOp",EDGE,"E25.MirrorCS"),sQuery(id+"F0.wireOp",EDGE,"E26.MirrorCS"),sQuery(id+"F0.wireOp",EDGE,"E27.MirrorCS"),sQuery(id+"F0.wireOp",EDGE,"E28.MirrorCS"),sQuery(id+"F0.wireOp",EDGE,"E29.MirrorCS"),sQuery(id+"F0.wireOp",EDGE,"E30.MirrorCS"),sQuery(id+"F0.wireOp",EDGE,"E31.MirrorCS"),sQuery(id+"F0.wireOp",EDGE,"E32.MirrorCS"),sQuery(id+"F0.wireOp",EDGE,"E33.MirrorCS"),sQuery(id+"F0.wireOp",EDGE,"E34.MirrorCS"),sQuery(id+"F0.wireOp",EDGE,"E35.MirrorCS"),sQuery(id+"F0.wireOp",EDGE,"E36.MirrorCS"),sQuery(id+"F0.wireOp",EDGE,"E44.MirrorCS"),sQuery(id+"F0.wireOp",EDGE,"E48.MirrorCS"),sQuery(id+"F0.wireOp",EDGE,"E53"),sQuery(id+"F0.wireOp",EDGE,"E54"),sQuery(id+"F0.wireOp",EDGE,"E57"),sQuery(id+"F0.wireOp",EDGE,"E58.filletArc"),sQuery(id+"F0.wireOp",EDGE,"E59.filletArc"),sQuery(id+"F0.wireOp",EDGE,"E60"),sQuery(id+"F0.wireOp",EDGE,"E61")])]});
            hole(context, id + "F5", {"style" : HoleStyle.C_SINK, "endStyle" : HoleEndStyle.THROUGH, "holeDiameter" : 19.05 * mm, "cSinkDiameter" : 31.75 * mm, "cSinkAngle" : 60 * degree, "majorDiameter" : 6.35 * mm, "isTappedThrough" : true, "tappedDepth" : 12.7 * mm, "tapClearance" : 3, "locations" : qUnion([Q0, Q1, Q2, Q3, Q4]), "scope" : qUnion([Q5])});
        }
        {
            var Q0;
            Q0=makeQuery(id+"F1.opRevolve","SWEPT_EDGE",EDGE,{"disambiguationData":[OSD([sQuery(id+"F0.wireOp",EDGE,"E57"),sQuery(id+"F0.wireOp",EDGE,"E60")])]});
            chamfer(context, id + "F6", {"entities" : qUnion([Q0]), "width" : 5.08 * mm, "tangentPropagation" : true});
        }
        {
            var Q0;
            Q0=makeQuery(id+"F1.opRevolve","SWEPT_EDGE",EDGE,{"disambiguationData":[OSD([sQuery(id+"F0.wireOp",EDGE,"E53"),sQuery(id+"F0.wireOp",EDGE,"E54")])]});
            chamfer(context, id + "F7", {"entities" : qUnion([Q0]), "width" : 12.7 * mm, "tangentPropagation" : true});
        }
        {
            var Q0;
            Q0=makeQuery(id+"F1.opRevolve","SWEPT_FACE",FACE,{"disambiguationData":[OSD([sQuery(id+"F0.wireOp",EDGE,"E0")])]});
            fillet(context, id + "F8", {"entities" : qUnion([Q0]), "radius" : 12.7 * mm, "tangentPropagation" : true, "allowEdgeOverflow" : false});
        }
    });
